FCSTD DOCUMENT  (FreeCAD 0.15R4671 (Git))
Label: Poliphemo
License: CreativeCommons Attribution-ShareAlike
LicenseURL: http://creativecommons.org/licenses/by-sa/4.0/
objects: Part::Cut×70, Part::Feature×40, Part::Cylinder×36, Part::FeaturePython×29, Part::Box×22, Part::MultiFuse×21, Sketcher::SketchObject×14, PartDesign::Pad×12, App::DocumentObjectGroup×12, Part::Fillet×6, Part::Prism×3, Part::Torus×2, Part::Extrusion×2, PartDesign::Revolution×2, Part::Offset×2, Part::Mirroring×1, Mesh::Feature×1
note: 276 computed .brp shape members not serialized (recipe doc carries the construction recipe); baked Part::Feature solids carry a one-line shape summary decoded from their .brp

FEATURE [Sketcher::SketchObject] Sketch
  Placement = pos=(0,0,0) rot=(1,0,0;1.5708rad)
  sketch-geometry (21):
    g0: LineSegment StartX=59.0543 StartY=-10.7909 StartZ=0 EndX=-13.0001 EndY=-10.7909 EndZ=0
    g1: LineSegment StartX=-15.0001 StartY=-12.7909 StartZ=0 EndX=-15.0001 EndY=-13.1898 EndZ=0
    g2: LineSegment StartX=-15 StartY=-20 StartZ=0 EndX=-18.8946 EndY=-20 EndZ=0
    g3: LineSegment StartX=-35 StartY=-13.1889 StartZ=0 EndX=-35 EndY=11.0101 EndZ=0
    g4: LineSegment StartX=-30 StartY=16.0101 StartZ=0 EndX=-9.59477 EndY=16.0101 EndZ=0
    g5: LineSegment StartX=39.6313 StartY=31.2232 StartZ=0 EndX=53.9362 EndY=56 EndZ=0
    g6: LineSegment StartX=74.9966 StartY=44.5054 StartZ=0 EndX=62.8248 EndY=20.8731 EndZ=0
    g7: LineSegment StartX=59.0543 StartY=5.31798 StartZ=0 EndX=59.0543 EndY=-10.7909 EndZ=0
    g8: Circle CenterX=-25 CenterY=-11.9899 CenterZ=0 NormalX=0 NormalY=0 NormalZ=1 Radius=2
    g9: Circle CenterX=64.3285 CenterY=50 CenterZ=0 NormalX=0 NormalY=0 NormalZ=1 Radius=2
    g10: Circle CenterX=35.461 CenterY=0 CenterZ=0 NormalX=0 NormalY=0 NormalZ=1 Radius=3.1
    g11: LineSegment [constr] StartX=35.461 StartY=0 StartZ=0 EndX=64.3285 EndY=50 EndZ=0
    g12: LineSegment [constr] StartX=51.5443 StartY=57.3809 StartZ=0 EndX=80.72 EndY=40.5364 EndZ=0
    g13: ArcOfCircle CenterX=64.3285 CenterY=50 CenterZ=0 NormalX=0 NormalY=0 NormalZ=1 Radius=12 StartAngle=5.80757 EndAngle=8.90118
    g14: ArcOfCircle CenterX=-30 CenterY=11.0101 CenterZ=0 NormalX=0 NormalY=0 NormalZ=1 Radius=5 StartAngle=1.5708 EndAngle=3.14159
    g15: ArcOfCircle CenterX=93.0258 CenterY=5.31798 CenterZ=0 NormalX=0 NormalY=0 NormalZ=1 Radius=33.9715 StartAngle=2.66598 EndAngle=3.14159
    g16: LineSegment StartX=1.09718 StartY=17.2548 StartZ=0 EndX=30.0327 EndY=24.0842 EndZ=0
    g17: ArcOfCircle CenterX=26.5676 CenterY=38.7656 CenterZ=0 NormalX=0 NormalY=0 NormalZ=1 Radius=15.0848 StartAngle=4.94417 EndAngle=5.75959
    g18: ArcOfCircle CenterX=-9.59477 CenterY=62.5551 CenterZ=0 NormalX=0 NormalY=0 NormalZ=1 Radius=46.545 StartAngle=4.71239 EndAngle=4.94417
    g19: ArcOfCircle CenterX=-25 CenterY=-11.9899 CenterZ=0 NormalX=0 NormalY=0 NormalZ=1 Radius=10.0716 StartAngle=3.26092 EndAngle=6.16376
    g20: ArcOfCircle CenterX=-13.0001 CenterY=-12.7909 CenterZ=0 NormalX=0 NormalY=0 NormalZ=1 Radius=2 StartAngle=1.5708 EndAngle=3.14159
  constraints (48):
    c: Horizontal(g0)
    c: Vertical(g1)
    c: Horizontal(g2)
    c: Vertical(g3)
    c: Horizontal(g4)
    c: Coincident(g7,g0)
    c: Radius(g8) = 2
    c: Radius(g9) = 2
    c: DistanceY(g-1,g9) = 50
    c: PointOnObject(g10,g-1)
    c: Radius(g10) = 3.1
    c: DistanceX(g-1,g8) = -25
    c: DistanceY(g-1,g8) = -11.9899
    c: DistanceX(g-1,g10) = 35.461
    c: DistanceY(g-1,g2) = -20
    c: Vertical(g7)
    c: DistanceX(g-1,g2) = -15
    c: Coincident(g11,g10)
    c: Coincident(g11,g9)
    c: DistanceY(g-1,g0) = -10.7909
    c: Angle(g11,g-1) = 2.0944
    c: Perpendicular(g11,g12)
    c: PointOnObject(g9,g12)
    c: Coincident(g13,g9)
    c: PointOnObject(g13,g5)
    c: PointOnObject(g5,g12)
    c: Tangent(g3,g14) = 1.5708
    c: Tangent(g4,g14) = 1.5708
    c: Tangent(g6,g15) = -1.5708
    c: Tangent(g7,g15) = -1.5708
    c: Tangent(g5,g13)
    c: Tangent(g6,g13)
    c: Coincident(g13,g6)
    c: Radius(g14) = 5
    c: Coincident(g5,g13)
    c: Radius(g13) = 12
    c: Tangent(g5,g17) = -1.5708
    c: Tangent(g16,g17) = -1.5708
    c: Tangent(g16,g18) = -1.5708
    c: Tangent(g4,g18) = -1.5708
    c: Coincident(g19,g8)
    c: PointOnObject(g2,g19)
    c: Coincident(g19,g1)
    c: Coincident(g3,g19)
    c: DistanceY(g4,g8) = -28
    c: Tangent(g1,g20) = -1.5708
    c: Tangent(g0,g20) = -1.5708
    c: Radius(g20) = 2
FEATURE [PartDesign::Pad] Pad
  Length = 4
  Length2 = 100
  Placement = pos=(0,0,0) rot=(1,0,0;1.5708rad)
  Sketch = -> Sketch
  Type = 0
FEATURE [Part::Box] Box  label="Cubo"
  Height = 30
  Length = 41.5
  Placement = pos=(4.2,-9,-19.6) rot=(0,0,1;0rad)
  Width = 20
FEATURE [Part::Cut] Cut
  Base = -> Pad
  Tool = -> Box
FEATURE [Sketcher::SketchObject] Sketch001
  Placement = pos=(0,0,0) rot=(0.57735,0.57735,0.57735;2.0944rad)
  sketch-geometry (5):
    g0: LineSegment StartX=-11.5774 StartY=37.7829 StartZ=0 EndX=-3.92366 EndY=37.7829 EndZ=0
    g1: LineSegment StartX=-3.92366 StartY=37.7829 StartZ=0 EndX=-3.92366 EndY=22.6692 EndZ=0
    g2: LineSegment StartX=-3.92366 StartY=22.6692 StartZ=0 EndX=-5.45233 EndY=33.3699 EndZ=0
    g3: LineSegment StartX=-7.03312 StartY=35.548 StartZ=0 EndX=-11.5774 EndY=37.7829 EndZ=0
    g4: ArcOfCircle CenterX=-8.30471 CenterY=32.9624 CenterZ=0 NormalX=0 NormalY=0 NormalZ=1 Radius=2.88134 StartAngle=0.141897 EndAngle=1.11373
  constraints (7):
    c: Horizontal(g0)
    c: Coincident(g0,g1)
    c: Vertical(g1)
    c: Coincident(g1,g2)
    c: Coincident(g3,g0)
    c: Tangent(g3,g4) = -1.5708
    c: Tangent(g2,g4) = -1.5708
FEATURE [PartDesign::Pad] Pad001
  Length = 3
  Length2 = 100
  Placement = pos=(0,0,0) rot=(0.57735,0.57735,0.57735;2.0944rad)
  Sketch = -> Sketch001
  Type = 0
FEATURE [Part::Fillet] Fillet
  Base = -> Pad001
  Edges = 6 edges r=1.1: [Edge9,Edge10,Edge12,Edge13,Edge14,Edge15]
  Placement = pos=(2,-33,4) rot=(0,0,1;0rad)
FEATURE [Part::FeaturePython] Clone  label="Clone of Fillet"  # Draft clone (typed FeaturePython)
  Objects = -> [Fillet]
  Placement = pos=(45.2816,0,3.93484) rot=(0,1,0;0.349066rad)
  Scale = (1,1,1)
FEATURE [Sketcher::SketchObject] Sketch002
  ExternalGeometry = -> [Cut]
  Placement = pos=(0,-4,0) rot=(1,0,0;1.5708rad)
  Support = -> Cut [Face5]
  sketch-geometry (2):
    g0: Circle CenterX=64.3285 CenterY=50 CenterZ=0 NormalX=0 NormalY=0 NormalZ=1 Radius=12
    g1: Circle CenterX=-25 CenterY=-11.9899 CenterZ=0 NormalX=0 NormalY=0 NormalZ=1 Radius=10.0716
  constraints (4):
    c: Coincident(g0,g-4)
    c: Coincident(g1,g-6)
    c: PointOnObject(g-6,g1)
    c: Radius(g0) = 12
FEATURE [PartDesign::Pad] Pad002
  Length = 13
  Length2 = 100
  Sketch = -> Sketch002
  Type = 0
FEATURE [Part::Cylinder] Cylinder  label="Cilindro"
  Angle = 360
  Height = 30
  Placement = pos=(-25,4,-12) rot=(1,0,0;1.5708rad)
  Radius = 2
FEATURE [Part::Cylinder] Cylinder001  label="Cilindro001"
  Angle = 360
  Height = 30
  Placement = pos=(64.33,4,50) rot=(1,0,0;1.5708rad)
  Radius = 2
FEATURE [Part::Cut] Cut001
  Base = -> Pad002
  Tool = -> Cylinder001
FEATURE [Part::Cut] Cut002
  Base = -> Cut001
  Tool = -> Cylinder
FEATURE [Part::MultiFuse] Fusion
  Shapes = -> [Cut002,Clone]
FEATURE [Part::Cylinder] Cylinder002  label="Cilindro002"
  Angle = 360
  Height = 30
  Placement = pos=(50.1,14,5.1) rot=(1,0,0;1.5708rad)
  Radius = 2
FEATURE [Part::Cylinder] Cylinder003  label="Cilindro003"
  Angle = 360
  Height = 30
  Placement = pos=(50.1,14,-5.1) rot=(1,0,0;1.5708rad)
  Radius = 2
FEATURE [Part::Cylinder] Cylinder004  label="Cilindro004"
  Angle = 360
  Height = 30
  Placement = pos=(-0.1,14,5.1) rot=(1,0,0;1.5708rad)
  Radius = 2
FEATURE [Part::Cylinder] Cylinder005  label="Cilindro005"
  Angle = 360
  Height = 30
  Placement = pos=(-0.1,14,-5.1) rot=(1,0,0;1.5708rad)
  Radius = 2
FEATURE [Part::Cut] Cut003
  Base = -> Fusion
  Tool = -> Cylinder002
FEATURE [Part::Cut] Cut004
  Base = -> Cut003
  Tool = -> Cylinder003
FEATURE [Part::Cut] Cut005
  Base = -> Cut004
  Tool = -> Cylinder004
FEATURE [Part::Cut] Cut006  label="preLatDer"
  Base = -> Cut005
  Tool = -> Cylinder005
FEATURE [Part::Prism] Prism  label="Prisma001"
  Circumradius = 3.35
  Height = 2.25
  Placement = pos=(0,-10,0) rot=(0,0,1;0rad)
  Polygon = 6
FEATURE [Part::Cylinder] Cylinder006  label="Cilindro023"
  Angle = 360
  Height = 30
  Placement = pos=(6e-12,-10,2.25) rot=(0,0,1;0rad)
  Radius = 2
FEATURE [Part::MultiFuse] Fusion001  label="taladroTuerca"
  Placement = pos=(-25,-17.1,-22) rot=(-1,0,0;1.5708rad)
  Shapes = -> [Prism,Cylinder006]
FEATURE [Part::FeaturePython] Clone001  label="Clone of taladroTuerca"  # Draft clone (typed FeaturePython)
  Objects = -> [Fusion001]
  Placement = pos=(64.33,-17.1,40) rot=(-1,0,0;1.5708rad)
  Scale = (1,1,1)
FEATURE [Part::FeaturePython] Clone002  label="Clone of taladroTuerca001"  # Draft clone (typed FeaturePython)
  Objects = -> [Fusion001]
  Placement = pos=(64.33,0.1,60) rot=(1,0,0;1.5708rad)
  Scale = (1,1,1)
FEATURE [Part::FeaturePython] Clone003  label="Clone of Clone of taladroTuerca001"  # Draft clone (typed FeaturePython)
  Objects = -> [Clone002]
  Placement = pos=(-25,0.1,-2) rot=(1,0,0;1.5708rad)
  Scale = (1,1,1)
FEATURE [Part::Cut] Cut007
  Base = -> Cut006
  Tool = -> Fusion001
FEATURE [Part::Cut] Cut008
  Base = -> Cut007
  Tool = -> Clone001
FEATURE [Part::Cut] Cut009
  Base = -> Cut008
  Tool = -> Clone002
FEATURE [Part::Cut] Cut010  label="preLateralDer"
  Base = -> Cut009
  Tool = -> Clone003
FEATURE [Part::Torus] Torus  label="Toro"
  Angle1 = -180
  Angle2 = 180
  Angle3 = 360
  Placement = pos=(64.3285,-16.5,50) rot=(1,0,0;1.5708rad)
  Radius1 = 7
  Radius2 = 1
FEATURE [Part::Torus] Torus001  label="Toro001"
  Angle1 = -180
  Angle2 = 180
  Angle3 = 360
  Placement = pos=(-25,-16.5,-11.9899) rot=(1,0,0;1.5708rad)
  Radius1 = 7
  Radius2 = 1
FEATURE [Part::MultiFuse] Fusion002
  Placement = pos=(-107.086,-40.5213,45) rot=(0,0,1;0rad)
  Shapes = -> [Cut010,Torus,Torus001]
FEATURE [Part::FeaturePython] Clone004  label="Clone of taladroTuerca004"  # WARN: FeaturePython — macro-defined, semantics opaque (R4)
  Placement = pos=(-24,12.1,16) rot=(1,0,0;1.5708rad)
  Scale = (1,1,1)
FEATURE [Part::FeaturePython] Clone005  label="Clone of Clone of taladroTuerca003"  # WARN: FeaturePython — macro-defined, semantics opaque (R4)
  Placement = pos=(49,3.1,41) rot=(1,0,0;1.5708rad)
  Scale = (1,1,1)
FEATURE [Part::Cut] Cut011
  Base = -> Fusion002
  Tool = -> Clone004
FEATURE [Part::Cut] Cut012  label="LateralDer"
  Base = -> Cut011
  Tool = -> Clone005
FEATURE [Part::FeaturePython] Clone006  label="Clone of preLatDerV5"  # Draft clone (typed FeaturePython)
  Objects = -> [Cut012]
  Scale = (1,1,1)
FEATURE [Part::Mirroring] Part__Mirroring  label="LateralIzq"
  Base = (20.7079,1.90735e-06,20.0487)
  Normal = (0,1,-1.19209e-07)
  Placement = pos=(0,64,0) rot=(0,0,1;0rad)
  Source = -> Clone006
FEATURE [App::DocumentObjectGroup] Grupo001  label="Gr_AuxLateral"
  Group = -> [Cut,Fillet]
FEATURE [App::DocumentObjectGroup] Grupo  label="GR_Laterales"
  Group = -> [Cut012,Part__Mirroring,Grupo001]
FEATURE [Part::Feature] Cut013  label="csLateralDer"
  shape: bbox 111.4 x 17.5 x 84.06 mm, 81 faces (baked)
FEATURE [Part::Feature] Part__Mirroring001  label="csLateralIzq"
  Placement = pos=(0,63,0) rot=(0,0,1;0rad)
  shape: bbox 111.4 x 17.5 x 84.06 mm, 81 faces (baked)
FEATURE [Part::Feature] Fusion003  label="csBaseV5"
  shape: bbox 114 x 63 x 24 mm, 132 faces (baked)
FEATURE [Part::Cylinder] Cylinder007  label="Cilindro024"
  Angle = 360
  Height = 19
  Placement = pos=(-46.35,14,0) rot=(0,0,1;0rad)
  Radius = 1
FEATURE [Part::Box] Box001  label="Cubo019"
  Height = 10
  Length = 9
  Placement = pos=(-31,0,-18) rot=(0,0,1;0rad)
  Width = 4
FEATURE [Part::Box] Box002  label="Cubo020"
  Height = 10
  Length = 9
  Placement = pos=(-31,59,-18) rot=(0,0,1;0rad)
  Width = 4
FEATURE [Part::Cut] Cut014
  Base = -> Fusion003
  Tool = -> Box001
FEATURE [Part::Cut] Cut015
  Base = -> Cut014
  Tool = -> Box002
FEATURE [Part::Box] Box003  label="Cubo021"
  Height = 20
  Length = 35
  Placement = pos=(6,14,0) rot=(0,0,1;0rad)
  Width = 35
FEATURE [Part::Fillet] Fillet001
  Base = -> Box003
  Edges = 4 edges r=10: [Edge1,Edge3,Edge5,Edge7]
FEATURE [Part::Cut] Cut016
  Base = -> Cut015
  Tool = -> Fillet001
FEATURE [Part::Cut] Cut017
  Base = -> Cut016
  Placement = pos=(2,-33,4) rot=(0,0,1;0rad)
  Tool = -> Cylinder007
FEATURE [Part::Box] Box004  label="Cubo022"
  Height = 5
  Length = 4
  Placement = pos=(-56.5,15.3,2) rot=(0,0,1;0rad)
  Width = 25
FEATURE [Part::Box] Box005  label="Cubo023"
  Height = 5
  Length = 4
  Placement = pos=(-40,15.3,2) rot=(0,0,1;0rad)
  Width = 25
FEATURE [Part::MultiFuse] Fusion004  label="Base"
  Placement = pos=(0,0,0) rot=(1,0,0;3.14159rad)
  Shapes = -> [Cut017,Box004,Box005]
FEATURE [Part::Box] Box006  label="Cubo001"
  Height = 4
  Length = 80
  Placement = pos=(-25.3,0,11) rot=(0,0,1;0rad)
  Width = 63
FEATURE [Part::Box] Box007  label="Cubo002"
  Height = 20
  Length = 9
  Placement = pos=(-5.3,0,-9) rot=(0,0,1;0rad)
  Width = 9
FEATURE [Part::FeaturePython] Clone007  label="Clone of Cubo002"  # Draft clone (typed FeaturePython)
  Objects = -> [Box007]
  Placement = pos=(-5.3,54,-9) rot=(0,0,1;0rad)
  Scale = (1,1,1)
FEATURE [Part::FeaturePython] Clone008  label="Clone of Cubo003"  # Draft clone (typed FeaturePython)
  Objects = -> [Box007]
  Placement = pos=(45.7,54,-9) rot=(0,0,1;0rad)
  Scale = (1,1,1)
FEATURE [Part::FeaturePython] Clone009  label="Clone of Cubo004"  # Draft clone (typed FeaturePython)
  Objects = -> [Box007]
  Placement = pos=(45.7,0,-9) rot=(0,0,1;0rad)
  Scale = (1,1,1)
FEATURE [Part::MultiFuse] Fusion005  label="preAlojaSer"
  Placement = pos=(0.25,0,0) rot=(0,0,1;0rad)
  Shapes = -> [Box006,Clone008,Clone007,Clone009,Box007]
FEATURE [Part::Cylinder] Cylinder008  label="Cilindro006"
  Angle = 360
  Height = 30
  Placement = pos=(50.1,14,5.1) rot=(1,0,0;1.5708rad)
  Radius = 2
FEATURE [Part::Cylinder] Cylinder009  label="Cilindro007"
  Angle = 360
  Height = 30
  Placement = pos=(50.1,14,-5.1) rot=(1,0,0;1.5708rad)
  Radius = 2
FEATURE [Part::Cylinder] Cylinder010  label="Cilindro008"
  Angle = 360
  Height = 30
  Placement = pos=(-0.1,14,5.1) rot=(1,0,0;1.5708rad)
  Radius = 2
FEATURE [Part::Cylinder] Cylinder011  label="Cilindro009"
  Angle = 360
  Height = 30
  Placement = pos=(-0.1,14,-5.1) rot=(1,0,0;1.5708rad)
  Radius = 2
FEATURE [Part::Cylinder] Cylinder012  label="Cilindro010"
  Angle = 360
  Height = 30
  Placement = pos=(50.1,76,5.1) rot=(1,0,0;1.5708rad)
  Radius = 2
FEATURE [Part::Cylinder] Cylinder013  label="Cilindro011"
  Angle = 360
  Height = 30
  Placement = pos=(50.1,76,-5.1) rot=(1,0,0;1.5708rad)
  Radius = 2
FEATURE [Part::Cylinder] Cylinder014  label="Cilindro012"
  Angle = 360
  Height = 30
  Placement = pos=(-0.1,76,5.1) rot=(1,0,0;1.5708rad)
  Radius = 2
FEATURE [Part::Cylinder] Cylinder015  label="Cilindro013"
  Angle = 360
  Height = 30
  Placement = pos=(-0.1,76,-5.1) rot=(1,0,0;1.5708rad)
  Radius = 2
FEATURE [Part::Cut] Cut018
  Base = -> Fusion005
  Tool = -> Cylinder008
FEATURE [Part::Cut] Cut019
  Base = -> Cut018
  Tool = -> Cylinder009
FEATURE [Part::Cut] Cut020
  Base = -> Cut019
  Placement = pos=(2,-33,4) rot=(0,0,1;0rad)
  Tool = -> Cylinder010
FEATURE [Part::Cut] Cut021
  Base = -> Cut020
  Placement = pos=(2,-33,4) rot=(0,0,1;0rad)
  Tool = -> Cylinder011
FEATURE [Part::Cut] Cut022
  Base = -> Cut021
  Tool = -> Cylinder012
FEATURE [Part::Cut] Cut023
  Base = -> Cut022
  Tool = -> Cylinder013
FEATURE [Part::Cut] Cut024
  Base = -> Cut023
  Tool = -> Cylinder014
FEATURE [Part::Cut] Cut025  label="preAlojaSer2"
  Base = -> Cut024
  Tool = -> Cylinder015
FEATURE [Part::Box] Box008  label="Hueco_Cuerpo_Tuerca_4"
  Height = 6
  Length = 62
  Placement = pos=(-6,3,2.1) rot=(0,0,1;0rad)
  Width = 3
FEATURE [Part::Box] Box009  label="Hueco_Cuerpo_Tuerca_005"
  Height = 6
  Length = 62
  Placement = pos=(-6,3,-8.1) rot=(0,0,1;0rad)
  Width = 3
FEATURE [Part::Box] Box010  label="Hueco_Cuerpo_Tuerca_006"
  Height = 6
  Length = 62
  Placement = pos=(-6,57,2.1) rot=(0,0,1;0rad)
  Width = 3
FEATURE [Part::Box] Box011  label="Hueco_Cuerpo_Tuerca_007"
  Height = 6
  Length = 62
  Placement = pos=(-6,57,-8.1) rot=(0,0,1;0rad)
  Width = 3
FEATURE [Part::Cut] Cut026
  Base = -> Cut025
  Tool = -> Box008
FEATURE [Part::Cut] Cut027
  Base = -> Cut026
  Tool = -> Box009
FEATURE [Part::Cut] Cut028
  Base = -> Cut027
  Tool = -> Box010
FEATURE [Part::Cut] Cut029  label="preAlojaSer3"
  Base = -> Cut028
  Tool = -> Box011
FEATURE [Part::Box] Box012  label="Cubo024"
  Height = 4
  Length = 35
  Placement = pos=(-59,0,11) rot=(0,0,1;0rad)
  Width = 63
FEATURE [Part::Cylinder] Cylinder016  label="Cilindro019"
  Angle = 360
  Height = 40
  Placement = pos=(-11.05,6,1) rot=(0,0,1;0rad)
  Radius = 2
FEATURE [Part::Cylinder] Cylinder017  label="Cilindro020"
  Angle = 360
  Height = 40
  Placement = pos=(-11.05,57,1) rot=(0,0,1;0rad)
  Radius = 2
FEATURE [Part::Cut] Cut030
  Base = -> Cut029
  Tool = -> Cylinder017
FEATURE [Part::Cut] Cut031
  Base = -> Cut030
  Tool = -> Cylinder016
FEATURE [Part::Box] Box013  label="Cubo011"
  Height = 12.5
  Length = 23.3
  Placement = pos=(-52.5,15.8,20.4) rot=(0,1,0;1.5708rad)
  Width = 24
FEATURE [Part::Feature] Pad003
  Placement = pos=(-12,31.5,7) rot=(0,0,1;0rad)
  shape: bbox 10 x 25 x 20 mm, 6 faces (baked)
FEATURE [Part::Cylinder] Cylinder018  label="Cilindro025"
  Angle = 360
  Height = 10
  Placement = pos=(-46,39.8,5) rot=(0,0,1;0rad)
  Radius = 2
FEATURE [Part::Fillet] Fillet002
  Base = -> Box012
  Edges = 2 edges r=20: [Edge1,Edge3]
FEATURE [Part::MultiFuse] Fusion006
  Shapes = -> [Cut031,Fillet002]
FEATURE [Part::Cut] Cut032
  Base = -> Fusion006
  Tool = -> Box013
FEATURE [Part::Cut] Cut033
  Base = -> Cut032
  Placement = pos=(0,0,-4) rot=(0,0,1;0rad)
  Tool = -> Pad003
FEATURE [Part::Cut] Cut034
  Base = -> Cut033
  Tool = -> Cylinder018
FEATURE [Part::Prism] Prism001  label="Prisma002"
  Circumradius = 3.35
  Height = 2.25
  Placement = pos=(0,-10,0) rot=(0,0,1;0rad)
  Polygon = 6
FEATURE [Part::Cylinder] Cylinder019  label="Cilindro026"
  Angle = 360
  Height = 30
  Placement = pos=(6e-12,-10,2.25) rot=(0,0,1;0rad)
  Radius = 2
FEATURE [Part::MultiFuse] Fusion007  label="taladroTuerca001"
  Placement = pos=(-24,12.1,12) rot=(1,0,0;1.5708rad)
  Shapes = -> [Prism001,Cylinder019]
FEATURE [Part::FeaturePython] Clone010  label="Clone of taladroTuerca005"  # Draft clone (typed FeaturePython)
  Objects = -> [Fusion007]
  Placement = pos=(-24,50.9,-8) rot=(-1,0,0;1.5708rad)
  Scale = (1,1,1)
FEATURE [Part::Box] Box014  label="Cubo012"
  Height = 13
  Length = 25
  Placement = pos=(-30,0,-6) rot=(0,0,1;0rad)
  Width = 12
FEATURE [Part::Box] Box015  label="Cubo013"
  Height = 3
  Length = 6
  Placement = pos=(-14.05,43.0988,1) rot=(0,0,1;0rad)
  Width = 22
FEATURE [Part::Box] Box016  label="Cubo014"
  Height = 13
  Length = 25
  Placement = pos=(-30.05,51,-6) rot=(0,0,1;0rad)
  Width = 12
FEATURE [Part::Box] Box017  label="Cubo015"
  Height = 3
  Length = 6
  Placement = pos=(-14.05,-6,1) rot=(0,0,1;0rad)
  Width = 22
FEATURE [Part::Cut] Cut035
  Base = -> Box016
  Tool = -> Box015
FEATURE [Part::Cut] Cut036
  Base = -> Box014
  Tool = -> Box017
FEATURE [Part::MultiFuse] Fusion008  label="taladroTuerca002"
  Placement = pos=(-11.05,-4,21.25) rot=(1,0,0;3.14159rad)
  Shapes = -> [Prism001,Cylinder019]
FEATURE [Part::FeaturePython] Clone011  label="Clone of taladroTuerca006"  # Draft clone (typed FeaturePython)
  Objects = -> [Fusion008]
  Placement = pos=(-11.05,47,21.25) rot=(1,0,0;3.14159rad)
  Scale = (1,1,1)
FEATURE [Part::Cut] Cut037
  Base = -> Cut036
  Tool = -> Fusion008
FEATURE [Part::Cut] Cut038
  Base = -> Cut035
  Tool = -> Clone011
FEATURE [Part::Cut] Cut039
  Base = -> Cut037
  Tool = -> Fusion007
FEATURE [Part::Cut] Cut040
  Base = -> Cut038
  Tool = -> Clone010
FEATURE [Part::MultiFuse] Fusion009  label="BaseV4"
  Shapes = -> [Cut034,Cut039,Cut040]
FEATURE [Part::Feature] Pad004
  Placement = pos=(-30.05,-0.115984,0.0102208) rot=(0.57735,0.57735,0.57735;2.0944rad)
  shape: bbox 25 x 12 x 7 mm, 8 faces (baked)
FEATURE [Part::Feature] Pad005
  Placement = pos=(-30.05,63.116,-19.0102) rot=(0.57735,-0.57735,0.57735;4.18879rad)
  shape: bbox 25 x 12 x 7 mm, 8 faces (baked)
FEATURE [Part::MultiFuse] Fusion010  label="BaseV5"
  Shapes = -> [Fusion009,Pad004,Pad005]
FEATURE [Sketcher::SketchObject] Sketch003
  Placement = pos=(-30,0,0) rot=(0.57735,0.57735,0.57735;2.0944rad)
  sketch-geometry (6):
    g0: LineSegment StartX=0.115984 StartY=-13.0102 StartZ=0 EndX=12.116 EndY=-13.0102 EndZ=0
    g1: LineSegment StartX=12.116 StartY=-13.0102 StartZ=0 EndX=8.96276 EndY=-9.857 EndZ=0
    g2: LineSegment StartX=8.96276 StartY=-9.857 StartZ=0 EndX=8.96276 EndY=-9.16345 EndZ=0
    g3: LineSegment StartX=8.96276 StartY=-9.16345 StartZ=0 EndX=12.116 EndY=-6.01022 EndZ=0
    g4: LineSegment StartX=12.116 StartY=-6.01022 StartZ=0 EndX=0.115984 EndY=-6.01022 EndZ=0
    g5: LineSegment StartX=0.115984 StartY=-6.01022 StartZ=0 EndX=0.115984 EndY=-13.0102 EndZ=0
  constraints (15):
    c: Coincident(g1,g2)
    c: Coincident(g2,g3)
    c: Coincident(g3,g4)
    c: Coincident(g4,g5)
    c: Coincident(g5,g0)
    c: Horizontal(g0)
    c: Coincident(g1,g0)
    c: Vertical(g5)
    c: DistanceY(g5) = -7
    c: Horizontal(g4)
    c: DistanceX(g0) = 12
    c: Equal(g0,g4)
    c: Angle(g4,g3) = 0.785398
    c: Angle(g1,g0) = 0.785398
    c: Vertical(g2)
FEATURE [PartDesign::Pad] Pad006  label="muesca"
  Length = 25
  Length2 = 100
  Placement = pos=(-30,0,0) rot=(0.57735,0.57735,0.57735;2.0944rad)
  Sketch = -> Sketch003
  Type = 0
FEATURE [App::DocumentObjectGroup] Grupo003  label="GR_AuxBase"
  Group = -> [Fusion010,Pad006]
FEATURE [App::DocumentObjectGroup] Grupo002  label="GR_Base"
  Group = -> [Grupo003,Fusion004]
FEATURE [Part::Feature] Fusion011  label="csBase"
  Placement = pos=(0,0,4) rot=(0,0,1;0rad)
  shape: bbox 114 x 63 x 24 mm, 155 faces (baked)
FEATURE [Part::Box] Box018  label="Cubo005"
  Height = 30
  Length = 60
  Placement = pos=(-5,0,14) rot=(0,0,1;0rad)
  Width = 63
FEATURE [Part::Box] Box019  label="Cubo006"
  Height = 39
  Length = 63
  Placement = pos=(-11,3,11) rot=(0,0,1;0rad)
  Width = 57
FEATURE [Part::Cut] Cut041  label="preAlojaPilas1"
  Base = -> Box018
  Placement = pos=(50,63,0) rot=(0,0,1;3.14159rad)
  Tool = -> Box019
FEATURE [Part::Box] Box020  label="Cubo018"
  Height = 5
  Length = 60
  Width = 63
FEATURE [Part::Feature] Face
  shape: bbox 41.8 x 19.8 x 2e-07 mm, 1 faces, 0 solids (baked)
FEATURE [Part::Extrusion] Extrude
  Base = -> Face
  Dir = (0,0,8)
  Placement = pos=(-6,92,-43) rot=(0,0,1;0rad)
  Solid = true
FEATURE [Part::Extrusion] Extrude001
  Base = -> Face
  Dir = (0,0,8)
  Placement = pos=(66,-29,-43) rot=(0,0,1;3.14159rad)
  Solid = true
FEATURE [Part::FeaturePython] Clone012  label="Clone of Extrude003"  # Draft clone (typed FeaturePython)
  Objects = -> [Extrude001]
  Placement = pos=(89,67.5,-43) rot=(0,0,-1;1.5708rad)
  Scale = (1,1,1)
FEATURE [Part::FeaturePython] Clone013  label="Clone of Extrude004"  # Draft clone (typed FeaturePython)
  Objects = -> [Extrude001]
  Placement = pos=(-29,-4.5,-43) rot=(0,0,1;1.5708rad)
  Scale = (1,1,1)
FEATURE [Part::Cut] Cut042
  Base = -> Box020
  Tool = -> Extrude
FEATURE [Part::Cut] Cut043
  Base = -> Cut042
  Tool = -> Extrude001
FEATURE [Part::Cut] Cut044
  Base = -> Cut043
  Tool = -> Clone012
FEATURE [Part::Cut] Cut045
  Base = -> Cut044
  Tool = -> Clone013
FEATURE [Part::Cylinder] Cylinder020  label="Cilindro027"
  Angle = 360
  Height = 10
  Placement = pos=(20.0282,41.5321,-3) rot=(0,0,1;0rad)
  Radius = 2
FEATURE [Part::Cylinder] Cylinder021  label="Cilindro028"
  Angle = 360
  Height = 10
  Placement = pos=(40.0282,41.5321,-3) rot=(0,0,1;0rad)
  Radius = 2
FEATURE [Part::Cylinder] Cylinder022  label="Cilindro021"
  Angle = 360
  Height = 10
  Placement = pos=(20.0282,21.5321,-3) rot=(0,0,1;0rad)
  Radius = 2
FEATURE [Part::Cylinder] Cylinder023  label="Cilindro022"
  Angle = 360
  Height = 10
  Placement = pos=(40.0282,21.5321,-3) rot=(0,0,1;0rad)
  Radius = 2
FEATURE [Part::Cut] Cut046
  Base = -> Cut045
  Tool = -> Cylinder020
FEATURE [Part::Cut] Cut047
  Base = -> Cut046
  Tool = -> Cylinder021
FEATURE [Part::Cut] Cut048
  Base = -> Cut047
  Tool = -> Cylinder022
FEATURE [Part::Cut] Cut049
  Base = -> Cut048
  Tool = -> Cylinder023
FEATURE [Part::Prism] Prism002  label="Prisma003"
  Circumradius = 3.35
  Height = 2.25
  Placement = pos=(0,-10,0) rot=(0,0,1;0rad)
  Polygon = 6
FEATURE [Part::Cylinder] Cylinder024  label="Cilindro029"
  Angle = 360
  Height = 10
  Placement = pos=(6e-12,-10,2.25) rot=(0,0,1;0rad)
  Radius = 2
FEATURE [Part::MultiFuse] Fusion012
  Placement = pos=(20.0282,31.5321,-0.05) rot=(0,0,1;0rad)
  Shapes = -> [Prism002,Cylinder024]
FEATURE [Part::FeaturePython] Clone014  label="Clone of Fusion003"  # Draft clone (typed FeaturePython)
  Objects = -> [Fusion012]
  Placement = pos=(40.0282,31.5321,-0.05) rot=(0,0,1;0rad)
  Scale = (1,1,1)
FEATURE [Part::FeaturePython] Clone015  label="Clone of Fusion004"  # Draft clone (typed FeaturePython)
  Objects = -> [Fusion012]
  Placement = pos=(40.0282,51.5321,-0.05) rot=(0,0,1;0rad)
  Scale = (1,1,1)
FEATURE [Part::FeaturePython] Clone016  label="Clone of Fusion005"  # Draft clone (typed FeaturePython)
  Objects = -> [Fusion012]
  Placement = pos=(20.0282,51.5321,-0.05) rot=(0,0,1;0rad)
  Scale = (1,1,1)
FEATURE [Part::Cut] Cut050
  Base = -> Cut049
  Tool = -> Fusion012
FEATURE [Part::Cut] Cut051
  Base = -> Cut050
  Tool = -> Clone014
FEATURE [Part::Cut] Cut052
  Base = -> Cut051
  Tool = -> Clone015
FEATURE [Part::Cut] Cut053  label="preXtap001"
  Base = -> Cut052
  Placement = pos=(-5,0,39) rot=(0,0,1;0rad)
  Tool = -> Clone016
FEATURE [Part::Cylinder] Cylinder025  label="Cilindro030"
  Angle = 180
  Height = 30
  Placement = pos=(-11,6,14) rot=(0,0,1;1.5708rad)
  Radius = 6
FEATURE [Part::Box] Box021  label="Cubo025"
  Height = 30
  Length = 12
  Placement = pos=(-5,0,14) rot=(0,0,1;1.5708rad)
  Width = 6
FEATURE [Part::Feature] Fusion013  label="csTaladro35x3"
  Placement = pos=(-11,6,47.5) rot=(1,0,0;3.14159rad)
  shape: bbox 5.8 x 5.8 x 38.5 mm, 5 faces (baked)
FEATURE [Part::MultiFuse] Fusion014
  Shapes = -> [Cylinder025,Box021]
FEATURE [Part::Cut] Cut054  label="FijaPieza2"
  Base = -> Fusion014
  Tool = -> Fusion013
FEATURE [Part::Feature] Cut055  label="FijaPieza1"
  Placement = pos=(0,51,0) rot=(0,0,1;0rad)
  shape: bbox 12 x 12 x 30 mm, 7 faces (baked)
FEATURE [Part::MultiFuse] Fusion015
  Shapes = -> [Cut041,Cut055,Cut054]
FEATURE [Part::MultiFuse] Fusion016
  Shapes = -> [Fusion015,Cut053]
FEATURE [Part::Fillet] Fillet003  label="TapaPilasV2"
  Base = -> Fusion016
  Edges = 2 edges r=5: [Edge39,Edge42]
FEATURE [Part::Feature] Fillet004  label="TapaPilasV003"
  shape: bbox 72 x 63 x 30 mm, 61 faces (baked)
FEATURE [Part::Feature] Clone017  label="ClonPoliphemoNom001"
  Placement = pos=(21,1,40) rot=(1,0,0;1.5708rad)
  shape: bbox 53.2 x 3 x 8.442 mm, 569 faces, 9 solids (baked)
FEATURE [Part::Cut] Cut056
  Base = -> Fillet004
  Placement = pos=(-0.05,0,-3) rot=(0,0,1;0rad)
  Tool = -> Clone017
FEATURE [Part::FeaturePython] Clone019  label="Clone of Clone of Clone of Clone of taladroTuerca"  # WARN: FeaturePython — macro-defined, semantics opaque (R4)
  Placement = pos=(49,59.9,21) rot=(-1,0,0;1.5708rad)
  Scale = (1,1,1)
FEATURE [Part::FeaturePython] Clone018  label="Clone of Clone of Clone of taladroTuerca002"  # Draft clone (typed FeaturePython)
  Objects = -> [Clone019]
  Placement = pos=(49,3.1,41) rot=(1,0,0;1.5708rad)
  Scale = (1,1,1)
FEATURE [Part::Cut] Cut057
  Base = -> Cut056
  Tool = -> Clone018
FEATURE [Part::Cut] Cut058  label="TapaAlojapilasV3"
  Base = -> Cut057
  Tool = -> Clone019
FEATURE [App::DocumentObjectGroup] Grupo004  label="GR_AlojapilasOld"
  Group = -> [Fillet003,Cut058]
FEATURE [Part::Feature] Fillet005  label="TapaPilasV004"
  shape: bbox 72 x 63 x 30 mm, 61 faces (baked)
FEATURE [Part::Feature] Clone020  label="ClonPoliphemoNom002"
  Placement = pos=(21,1,40) rot=(1,0,0;1.5708rad)
  shape: bbox 53.2 x 3 x 8.442 mm, 569 faces, 9 solids (baked)
FEATURE [Part::Cut] Cut059
  Base = -> Fillet005
  Placement = pos=(-2.05,33,-3) rot=(0,0,1;0rad)
  Tool = -> Clone020
FEATURE [Part::FeaturePython] Clone022  label="Clone of Clone of Clone of Clone of taladroTuerca001"  # WARN: FeaturePython — macro-defined, semantics opaque (R4)
  Placement = pos=(47,92.75,17) rot=(-1,0,0;1.5708rad)
  Scale = (1,1,1)
FEATURE [Part::FeaturePython] Clone021  label="Clone of Clone of Clone of taladroTuerca003"  # Draft clone (typed FeaturePython)
  Objects = -> [Clone022]
  Placement = pos=(47,36.25,37) rot=(1,0,0;1.5708rad)
  Scale = (1,1,1)
FEATURE [Part::Cut] Cut060
  Base = -> Cut059
  Tool = -> Clone021
FEATURE [Part::Cut] Cut061  label="TapaAlojapilasV4"
  Base = -> Cut060
  Placement = pos=(2,-33,4) rot=(0,0,1;0rad)
  Tool = -> Clone022
FEATURE [Part::Feature] Cut062  label="csAlojapilas"
  Placement = pos=(2,-33,4) rot=(0,0,1;0rad)
  shape: bbox 72 x 65 x 30 mm, 639 faces (baked)
FEATURE [App::DocumentObjectGroup] Grupo005  label="GR_AlojaPilas"
  Group = -> [Grupo004,Cut061]
FEATURE [Sketcher::SketchObject] Sketch004
  Placement = pos=(0,0,0) rot=(0.57735,0.57735,0.57735;2.0944rad)
  sketch-geometry (6):
    g0: LineSegment StartX=2.1 StartY=-10 StartZ=0 EndX=2.1 EndY=4 EndZ=0
    g1: LineSegment StartX=2.1 StartY=4 StartZ=0 EndX=3.5 EndY=4 EndZ=0
    g2: LineSegment StartX=3.5 StartY=4 StartZ=0 EndX=3.5 EndY=10 EndZ=0
    g3: LineSegment StartX=3.5 StartY=10 StartZ=0 EndX=13.8 EndY=10 EndZ=0
    g4: LineSegment StartX=13.8 StartY=10 StartZ=0 EndX=13.8 EndY=-10 EndZ=0
    g5: LineSegment StartX=13.8 StartY=-10 StartZ=0 EndX=2.1 EndY=-10 EndZ=0
  constraints (18):
    c: Coincident(g0,g1)
    c: Coincident(g1,g2)
    c: Coincident(g2,g3)
    c: Coincident(g3,g4)
    c: Coincident(g4,g5)
    c: Coincident(g5,g0)
    c: Horizontal(g5)
    c: Horizontal(g3)
    c: Vertical(g4)
    c: Vertical(g2)
    c: Vertical(g0)
    c: Horizontal(g1)
    c: DistanceY(g3,g4) = -20
    c: DistanceX(g-1,g4) = 13.8
    c: DistanceX(g-1,g0) = 2.1
    c: DistanceX(g-1,g2) = 3.5
    c: DistanceY(g2) = 6
    c: Symmetric(g3,g4,g-1)
FEATURE [PartDesign::Revolution] Revolution
  Angle = 360
  Axis = (0,0,1)
  Base = (0,0,0)
  Placement = pos=(0,0,0) rot=(0.57735,0.57735,0.57735;2.0944rad)
  ReferenceAxis = -> Sketch004 [V_Axis]
  Reversed = true
  Sketch = -> Sketch004
FEATURE [Sketcher::SketchObject] Sketch005
  Placement = pos=(0,0,-15) rot=(0,0,1;0rad)
  sketch-geometry (2):
    g0: Circle CenterX=0 CenterY=0 CenterZ=0 NormalX=0 NormalY=0 NormalZ=1 Radius=13.8
    g1: Circle CenterX=0 CenterY=0 CenterZ=0 NormalX=0 NormalY=0 NormalZ=1 Radius=17
  constraints (3):
    c: Coincident(g0,g-1)
    c: Radius(g0) = 13.8
    c: Radius(g1) = 17
FEATURE [PartDesign::Pad] Pad007
  Length = 30
  Length2 = 100
  Placement = pos=(0,0,-15) rot=(0,0,1;0rad)
  Sketch = -> Sketch005
  Type = 0
FEATURE [Part::FeaturePython] Clone023  label="Clone of Pad001"  # WARN: FeaturePython — macro-defined, semantics opaque (R4)
  Placement = pos=(0,0,-15) rot=(0,0,1;0rad)
  Scale = (1,1,1)
FEATURE [Part::FeaturePython] Array  # Draft array (typed FeaturePython)
  Angle = 360
  ArrayType = 1
  Axis = (0,0,1)
  Base = -> Clone023
  Center = (0,0,0)
  Fuse = false
  IntervalAxis = (0,0,0)
  IntervalX = (1,0,0)
  IntervalY = (0,1,0)
  IntervalZ = (0,0,0)
  NumberPolar = 8
  NumberX = 2
  NumberY = 2
  NumberZ = 1
FEATURE [Part::MultiFuse] Fusion017
  Shapes = -> [Pad007,Array]
FEATURE [Part::Cut] Cut063
  Base = -> Revolution
  Tool = -> Fusion017
FEATURE [Part::Fillet] Fillet006  label="ruedaPeq26"
  Base = -> Cut063
  Edges = 16 edges r=2.6: [Edge37,Edge43,Edge45,Edge51,Edge53,Edge59,Edge61,Edge67,Edge69,Edge75,Edge76,Edge83,Edge84,Edge91,Edge92,Edge99]
FEATURE [Part::Cylinder] Cylinder026  label="Cilindro031"
  Angle = 360
  Height = 1
  Placement = pos=(0,0,-11) rot=(0,0,1;0rad)
  Radius = 14.5
FEATURE [Part::Cylinder] Cylinder027  label="Cilindro032"
  Angle = 360
  Height = 10
  Placement = pos=(0,0,-16) rot=(0,0,1;0rad)
  Radius = 2.1
FEATURE [Part::Cut] Cut064
  Base = -> Cylinder026
  Tool = -> Cylinder027
FEATURE [Part::Cylinder] Cylinder028  label="Cilindro033"
  Angle = 360
  Height = 1
  Placement = pos=(0,0,-11) rot=(0,0,1;0rad)
  Radius = 14.5
FEATURE [Part::Cylinder] Cylinder029  label="Cilindro034"
  Angle = 360
  Height = 10
  Placement = pos=(0,0,-16) rot=(0,0,1;0rad)
  Radius = 3.5
FEATURE [Part::Cut] Cut065
  Base = -> Cylinder028
  Placement = pos=(0,0,21) rot=(0,0,1;0rad)
  Tool = -> Cylinder029
FEATURE [Part::FeaturePython] Clone024  label="Clone of ruedaPeq26"  # Draft clone (typed FeaturePython)
  Objects = -> [Fillet006]
  Scale = (1,1,1)
FEATURE [Part::MultiFuse] Fusion018  label="ruedaDentPeqTopes"
  Shapes = -> [Cut064,Cut065,Clone024]
FEATURE [App::DocumentObjectGroup] Grupo006  label="GR_RuedaPeq"
  Group = -> [Fillet006,Fusion018]
FEATURE [Part::Feature] Fusion019  label="csruedaDentPeq1"
  Placement = pos=(-25,-28.7,-11.9899) rot=(1,0,0;1.5708rad)
  shape: bbox 29 x 22 x 29 mm, 57 faces (baked)
FEATURE [Part::Feature] Fusion020  label="csruedaDentPeq2"
  Placement = pos=(64.3285,-28.7,50) rot=(1,0,0;1.5708rad)
  shape: bbox 29 x 22 x 29 mm, 57 faces (baked)
FEATURE [Part::Feature] Fusion021  label="csruedaDentPeq3"
  Placement = pos=(64.3285,91.7,50) rot=(0,0.707107,0.707107;3.14159rad)
  shape: bbox 29 x 22 x 29 mm, 57 faces (baked)
FEATURE [Part::Feature] Fusion022  label="csruedaDentPeq4"
  Placement = pos=(-25,91.7,-11.9899) rot=(0,0.707107,0.707107;3.14159rad)
  shape: bbox 29 x 22 x 29 mm, 57 faces (baked)
FEATURE [Part::Feature] Compound  label="ServoMG90S001"
  Placement = pos=(-32.1,25.8,42.7) rot=(0.57735,-0.57735,-0.57735;4.18879rad)
  shape: bbox 12.4 x 30.2 x 32.5 mm, 32 faces, 2 solids (baked)
FEATURE [Part::Feature] Compound001  label="ServoMG90S"
  Placement = pos=(-46.3,27.2,-0.9) rot=(0,0,-1;1.5708rad)
  shape: bbox 12.4 x 32.5 x 30.2 mm, 32 faces, 2 solids (baked)
FEATURE [Part::Feature] Cut066  label="forTilt002"
  Placement = pos=(-46.3,32.4,26.3) rot=(0.57735,-0.57735,-0.57735;2.0944rad)
  shape: bbox 50.58 x 52.96 x 11 mm, 101 faces (baked)
FEATURE [Part::Feature] Fusion023  label="prePortaCam003"
  Placement = pos=(-48.3,31.9,26.25) rot=(0,0,-1;1.5708rad)
  shape: bbox 13.33 x 53.91 x 19.33 mm, 65 faces (baked)
FEATURE [Part::Feature] Pad008  label="csSeparaPlaca"
  Placement = pos=(24.9782,31.5321,45) rot=(0,0,1;0rad)
  shape: bbox 28.03 x 28 x 3 mm, 18 faces (baked)
FEATURE [Part::Feature] Fusion024  label="csPixy"
  Placement = pos=(-72.3,31.901,42.2219) rot=(0.57735,-0.57735,-0.57735;2.0944rad)
  shape: bbox 22.9 x 53.85 x 50.8 mm, 52 faces (baked)
FEATURE [Part::Feature] Compound002  label="csServo-SM-S4303R_I"
  Placement = pos=(24.95,24.9,0) rot=(1,0,0;1.5708rad)
  shape: bbox 60.12 x 46.3 x 21.13 mm, 542 faces, 7 solids (baked)
FEATURE [Part::Feature] Compound003  label="Servo-SM-S4303R002"
  Placement = pos=(25.05,38.1,0) rot=(-1,0,0;1.5708rad)
  shape: bbox 60.12 x 46.3 x 21.13 mm, 542 faces, 7 solids (baked)
FEATURE [Sketcher::SketchObject] Sketch006
  Placement = pos=(0,0,0) rot=(-1,0,0;1.5708rad)
  sketch-geometry (7):
    g0: LineSegment StartX=4.5 StartY=12 StartZ=0 EndX=4.5 EndY=6 EndZ=0
    g1: LineSegment StartX=4.5 StartY=6 StartZ=0 EndX=17 EndY=6 EndZ=0
    g2: LineSegment StartX=20 StartY=3 StartZ=0 EndX=20 EndY=-12 EndZ=0
    g3: LineSegment StartX=20 StartY=-12 StartZ=0 EndX=26.5 EndY=-12 EndZ=0
    g4: LineSegment StartX=26.5 StartY=12 StartZ=0 EndX=4.5 EndY=12 EndZ=0
    g5: ArcOfCircle CenterX=17 CenterY=3 CenterZ=0 NormalX=0 NormalY=0 NormalZ=1 Radius=3 StartAngle=0 EndAngle=1.5708
    g6: LineSegment StartX=26.5 StartY=12 StartZ=0 EndX=26.5 EndY=-12 EndZ=0
  constraints (19):
    c: Vertical(g0)
    c: Coincident(g0,g1)
    c: Horizontal(g1)
    c: Vertical(g2)
    c: Coincident(g2,g3)
    c: Horizontal(g3)
    c: Coincident(g4,g0)
    c: Horizontal(g4)
    c: Symmetric(g4,g3,g-1)
    c: DistanceY(g0) = -6
    c: DistanceY(g4,g3) = -24
    c: DistanceX(g-1,g0) = 4.5
    c: DistanceX(g-1,g2) = 20
    c: DistanceX(g-1,g4) = 26.5
    c: Tangent(g1,g5) = 1.5708
    c: Tangent(g2,g5) = 1.5708
    c: Radius(g5) = 3
    c: Coincident(g6,g4)
    c: Coincident(g6,g3)
FEATURE [PartDesign::Revolution] Revolution001
  Angle = 360
  Axis = (0,0,-1)
  Base = (0,0,0)
  Placement = pos=(0,0,0) rot=(-1,0,0;1.5708rad)
  ReferenceAxis = -> Sketch006 [V_Axis]
  Reversed = true
  Sketch = -> Sketch006
FEATURE [Part::Feature] Fusion025  label="horn-body-003"
  Placement = pos=(0,0,-9.8) rot=(0,0,1;0rad)
  shape: bbox 38.8 x 38.8 x 32 mm, 26 faces (baked)
FEATURE [Sketcher::SketchObject] Sketch007
  Placement = pos=(0,0,-15) rot=(0,0,1;0rad)
  sketch-geometry (2):
    g0: Circle CenterX=0 CenterY=0 CenterZ=0 NormalX=0 NormalY=0 NormalZ=1 Radius=26.5
    g1: Circle CenterX=0 CenterY=0 CenterZ=0 NormalX=0 NormalY=0 NormalZ=1 Radius=35
  constraints (3):
    c: Coincident(g0,g-1)
    c: Radius(g0) = 26.5
    c: Radius(g1) = 35
FEATURE [PartDesign::Pad] Pad009
  Length = 30
  Length2 = 100
  Placement = pos=(0,0,-15) rot=(0,0,1;0rad)
  Sketch = -> Sketch007
  Type = 0
FEATURE [Sketcher::SketchObject] Sketch008
  sketch-geometry (8):
    g0: LineSegment StartX=28.5 StartY=2 StartZ=0 EndX=31.5 EndY=1.5 EndZ=0
    g1: LineSegment StartX=31.5 StartY=1.5 StartZ=0 EndX=31.5 EndY=-1.5 EndZ=0
    g2: LineSegment StartX=31.5 StartY=-1.5 StartZ=0 EndX=28.5 EndY=-2 EndZ=0
    g3: LineSegment StartX=28.5 StartY=2 StartZ=0 EndX=26.5 EndY=2 EndZ=0
    g4: LineSegment StartX=26.5 StartY=2 StartZ=0 EndX=23.5 EndY=1.5 EndZ=0
    g5: LineSegment StartX=23.5 StartY=1.5 StartZ=0 EndX=23.5 EndY=-1.5 EndZ=0
    g6: LineSegment StartX=23.5 StartY=-1.5 StartZ=0 EndX=26.5 EndY=-2 EndZ=0
    g7: LineSegment StartX=26.5 StartY=-2 StartZ=0 EndX=28.5 EndY=-2 EndZ=0
  constraints (23):
    c: Coincident(g0,g1)
    c: Vertical(g1)
    c: Coincident(g1,g2)
    c: Symmetric(g0,g2,g-1)
    c: Symmetric(g1,g0,g-1)
    c: DistanceY(g1) = -3
    c: DistanceX(g2,g1) = 3
    c: DistanceX(g-1,g2) = 28.5
    c: Coincident(g0,g3)
    c: Horizontal(g3)
    c: Coincident(g3,g4)
    c: Coincident(g4,g5)
    c: Vertical(g5)
    c: Coincident(g5,g6)
    c: Coincident(g6,g7)
    c: Coincident(g7,g2)
    c: Horizontal(g7)
    c: Symmetric(g3,g6,g-1)
    c: Symmetric(g4,g5,g-1)
    c: DistanceX(g3) = -2
    c: Equal(g1,g5)
    c: DistanceY(g0,g2) = -4
    c: DistanceX(g4,g3) = 3
FEATURE [PartDesign::Pad] Pad010
  Length = 30
  Length2 = 100
  Sketch = -> Sketch008
  Type = 0
FEATURE [Part::FeaturePython] Clone025  label="Clone of Pad002"  # Draft clone (typed FeaturePython)
  Objects = -> [Pad010]
  Placement = pos=(0,0,-15) rot=(0,0,1;0rad)
  Scale = (1,1,1)
FEATURE [Part::FeaturePython] Array001  # Draft array (typed FeaturePython)
  Angle = 360
  ArrayType = 1
  Axis = (0,0,1)
  Base = -> Clone025
  Center = (0,0,0)
  Fuse = false
  IntervalAxis = (0,0,0)
  IntervalX = (1,0,0)
  IntervalY = (0,1,0)
  IntervalZ = (0,0,0)
  NumberPolar = 16
  NumberX = 2
  NumberY = 2
  NumberZ = 1
FEATURE [Part::MultiFuse] Fusion026
  Shapes = -> [Pad009,Array001]
FEATURE [Part::Cut] Cut067
  Base = -> Revolution001
  Tool = -> Fusion025
FEATURE [Part::Cut] Cut068
  Base = -> Cut067
  Tool = -> Fusion026
FEATURE [Part::Fillet] Fillet007  label="ruedaDentServoV2_26"
  Base = -> Cut068
  Edges = 32 edges r=2.6: [Edge68,Edge71,Edge73,Edge79,Edge81,Edge87,Edge89,Edge95,Edge97,Edge103,Edge105,Edge111,Edge113,Edge119,Edge121,Edge127,Edge129,Edge135,Edge137,Edge143,Edge145,Edge151,Edge153,Edge159,Edge161,Edge167,Edge169,Edge175,Edge177,Edge183,Edge185,Edge191]
FEATURE [Part::Cylinder] Cylinder030  label="preTopeCorrea"
  Angle = 360
  Height = 2
  Placement = pos=(0,0,-12) rot=(0,0,1;0rad)
  Radius = 28.5
FEATURE [Part::Cylinder] Cylinder031  label="Taladro"
  Angle = 360
  Height = 10
  Placement = pos=(0,0,-15) rot=(0,0,1;0rad)
  Radius = 4.5
FEATURE [Part::Cut] Cut069  label="tope"
  Base = -> Cylinder030
  Tool = -> Cylinder031
FEATURE [Part::MultiFuse] Fusion027  label="ruedaDentServoV4"
  Shapes = -> [Fillet007,Cut069]
FEATURE [App::DocumentObjectGroup] Grupo007  label="GR_RuedaServo"
  Group = -> [Pad010,Fusion027]
FEATURE [Part::Feature] Fusion029  label="csRuedaDentServoD"
  Placement = pos=(35.6,92,0) rot=(-1,0,0;1.5708rad)
  shape: bbox 57 x 24 x 57 mm, 132 faces (baked)
FEATURE [Part::Feature] Fusion030  label="csRuedaDentServoI"
  Placement = pos=(35.5,-29,0) rot=(0,-0.707107,0.707107;3.14159rad)
  shape: bbox 57 x 24 x 57 mm, 132 faces (baked)
FEATURE [Part::Cylinder] Cylinder032  label="Cilindro035"
  Angle = 360
  Height = 2
  Radius = 28.5
FEATURE [Sketcher::SketchObject] Sketch009
  sketch-geometry (11):
    g0: LineSegment [constr] StartX=-15.0987 StartY=0 StartZ=0 EndX=15.0987 EndY=0 EndZ=0
    g1: ArcOfCircle CenterX=0 CenterY=-16.4544 CenterZ=0 NormalX=0 NormalY=0 NormalZ=1 Radius=22.332 StartAngle=0.828339 EndAngle=1.43871
    g2: ArcOfCircle CenterX=0 CenterY=16.4544 CenterZ=0 NormalX=0 NormalY=0 NormalZ=1 Radius=22.332 StartAngle=3.96993 EndAngle=4.6609
    g3: ArcOfCircle CenterX=0 CenterY=-16.4544 CenterZ=0 NormalX=0 NormalY=0 NormalZ=1 Radius=23.8811 StartAngle=0.748374 EndAngle=2.39322
    g4: ArcOfCircle CenterX=0 CenterY=16.4544 CenterZ=0 NormalX=0 NormalY=0 NormalZ=1 Radius=24.1614 StartAngle=3.90238 EndAngle=4.6648
    g5: ArcOfCircle CenterX=0 CenterY=-16.4544 CenterZ=0 NormalX=0 NormalY=0 NormalZ=1 Radius=22.332 StartAngle=1.70288 EndAngle=2.31325
    g6: LineSegment StartX=-1.1494 StartY=-5.84798 StartZ=0 EndX=-1.1494 EndY=-7.67959 EndZ=0
    g7: LineSegment StartX=1.31676 StartY=-5.83873 StartZ=0 EndX=1.31676 EndY=-7.67104 EndZ=0
    g8: ArcOfCircle CenterX=0 CenterY=16.4544 CenterZ=0 NormalX=0 NormalY=0 NormalZ=1 Radius=22.332 StartAngle=4.77139 EndAngle=5.45485
    g9: ArcOfCircle CenterX=0 CenterY=16.4544 CenterZ=0 NormalX=0 NormalY=0 NormalZ=1 Radius=24.1614 StartAngle=4.76691 EndAngle=5.5224
    g10: ArcOfCircle CenterX=0 CenterY=0.886253 CenterZ=0 NormalX=0 NormalY=0 NormalZ=1 Radius=5.62671 StartAngle=2.12083 EndAngle=7.30395
  constraints (29):
    c: Horizontal(g0)
    c: PointOnObject(g0,g-1)
    c: Coincident(g5,g0)
    c: Coincident(g1,g0)
    c: Equal(g1,g2)
    c: Coincident(g2,g0)
    c: Coincident(g0,g8)
    c: Coincident(g1,g3)
    c: Coincident(g2,g4)
    c: PointOnObject(g2,g-2)
    c: Coincident(g9,g3)
    c: Equal(g1,g5)
    c: Coincident(g1,g5)
    c: PointOnObject(g4,g3)
    c: Coincident(g3,g4)
    c: Vertical(g6)
    c: Parallel(g6,g7)
    c: Equal(g2,g8)
    c: Coincident(g2,g8)
    c: Equal(g4,g9)
    c: Coincident(g4,g9)
    c: Coincident(g6,g4)
    c: Coincident(g7,g9)
    c: Coincident(g7,g8)
    c: Coincident(g6,g2)
    c: DistanceX(g3,g3) = 35
    c: PointOnObject(g10,g-2)
    c: Coincident(g10,g5)
    c: Coincident(g1,g10)
FEATURE [PartDesign::Pad] Pad011  label="ojoMolde"
  Length = 2
  Length2 = 100
  Sketch = -> Sketch009
  Type = 0
FEATURE [Part::Cylinder] Cylinder033  label="Cilindro036"
  Angle = 360
  Height = 10
  Radius = 20
FEATURE [Part::Cylinder] Cylinder034  label="Cilindro037"
  Angle = 360
  Height = 10
  Radius = 19
FEATURE [Part::Cut] Cut070
  Base = -> Cylinder033
  Placement = pos=(0,0,-10) rot=(0,0,1;0rad)
  Tool = -> Cylinder034
FEATURE [Sketcher::SketchObject] Sketch010
  Placement = pos=(0,0,0) rot=(0.57735,0.57735,0.57735;2.0944rad)
  sketch-geometry (3):
    g0: LineSegment StartX=0 StartY=10 StartZ=0 EndX=-5.37675 EndY=-10.0663 EndZ=0
    g1: LineSegment StartX=-5.37675 StartY=-10.0663 StartZ=0 EndX=5.37675 EndY=-10.0663 EndZ=0
    g2: LineSegment StartX=5.37675 StartY=-10.0663 StartZ=0 EndX=0 EndY=10 EndZ=0
  constraints (9):
    c: PointOnObject(g0,g-2)
    c: Coincident(g0,g1)
    c: Horizontal(g1)
    c: Coincident(g1,g2)
    c: Coincident(g2,g0)
    c: Symmetric(g1,g0,g-2)
    c: DistanceY(g-1,g0) = 10
    c: Angle(g0,g2) = 0.523599
    c: DistanceY(g0,g1) = -20.0663
FEATURE [PartDesign::Pad] Pad012  label="Corte"
  Length = 100
  Length2 = 100
  Placement = pos=(0,0,0) rot=(0.57735,0.57735,0.57735;2.0944rad)
  Sketch = -> Sketch010
  Type = 0
FEATURE [Part::FeaturePython] Clone026  label="Clone of Pad"  # Draft clone (typed FeaturePython)
  Objects = -> [Pad012]
  Placement = pos=(-44,0,-10) rot=(0.57735,0.57735,0.57735;2.0944rad)
  Scale = (1,1,1)
FEATURE [Part::FeaturePython] Clone027  label="Clone of Pad003"  # Draft clone (typed FeaturePython)
  Objects = -> [Pad012]
  Placement = pos=(0,-44,-10) rot=(0,0.707107,0.707107;3.14159rad)
  Scale = (1,1,1)
FEATURE [Part::Cut] Cut071
  Base = -> Cut070
  Tool = -> Clone026
FEATURE [Part::Cut] Cut072
  Base = -> Cut071
  Tool = -> Clone027
FEATURE [Part::Feature] Pad013
  Placement = pos=(0,0,-3) rot=(0,0,1;0rad)
  shape: bbox 43.93 x 22.27 x 10 mm, 12 faces (baked)
FEATURE [Part::Offset] Offset  label="Hueco001"
  Fill = false
  Intersection = false
  Join = 2
  Mode = 0
  Placement = pos=(0,0,-3) rot=(0,0,1;0rad)
  SelfIntersection = false
  Source = -> Pad013
  Value = 0.2
FEATURE [Part::Feature] Pad014  label="Pad018"
  Placement = pos=(0,0,-3) rot=(0,0,1;0rad)
  shape: bbox 35 x 15.11 x 10 mm, 12 faces (baked)
FEATURE [Part::Offset] Offset001  label="Hueco"
  Fill = false
  Intersection = false
  Join = 2
  Mode = 0
  Placement = pos=(0,0,-3) rot=(0,0,1;0rad)
  SelfIntersection = false
  Source = -> Pad014
  Value = 0.22
FEATURE [Part::Cut] Cut073
  Base = -> Cylinder032
  Tool = -> Offset001
FEATURE [Part::MultiFuse] Fusion031  label="TapaCubos"
  Placement = pos=(0,0,0) rot=(1,0,0;3.14159rad)
  Shapes = -> [Cut072,Cut073]
FEATURE [Part::Cylinder] Cylinder035  label="Cilindro038"
  Angle = 360
  Height = 0.8
  Radius = 18.7
FEATURE [Part::Feature] Pad015  label="Pieza"
  Placement = pos=(0,0,0.8) rot=(0,0,1;0rad)
  shape: bbox 35 x 15.11 x 2 mm, 12 faces (baked)
FEATURE [Part::MultiFuse] Fusion032  label="Decoracion"
  Placement = pos=(0,0,0.8) rot=(1,0,0;3.14159rad)
  Shapes = -> [Cylinder035,Pad015]
FEATURE [App::DocumentObjectGroup] Grupo008  label="GR_TapaCubos"
  Group = -> [Pad011,Pad012,Offset,Fusion031,Fusion032]
FEATURE [Part::Feature] Fusion033  label="csOjoDecoracionI"
  Placement = pos=(35.5,-41,0) rot=(1,0,0;1.5708rad)
  shape: bbox 37.4 x 2.8 x 37.4 mm, 14 faces (baked)
FEATURE [Part::Feature] Fusion034  label="csTapaCubosI"
  Placement = pos=(35.5,-41,0) rot=(1,0,0;1.5708rad)
  shape: bbox 57 x 12 x 57 mm, 34 faces (baked)
FEATURE [Part::Feature] Fusion035  label="csOjoDecoracionD"
  Placement = pos=(35.6,104,0) rot=(0,0.707107,0.707107;3.14159rad)
  shape: bbox 37.4 x 2.8 x 37.4 mm, 14 faces (baked)
FEATURE [Part::Feature] Fusion036  label="csTapaCubosD"
  Placement = pos=(35.6,104,0) rot=(0,0.707107,0.707107;3.14159rad)
  shape: bbox 57 x 12 x 57 mm, 34 faces (baked)
FEATURE [Part::Feature] Compound004  label="battery-holder001"
  Placement = pos=(26,34,28) rot=(0,0,1;1.5708rad)
  shape: bbox 60.07 x 51.23 x 30.51 mm, 1148 faces, 59 solids (baked)
FEATURE [Mesh::Feature] zum_bt_  label="zum_bt_328"
  Placement = pos=(59,58,50) rot=(0,0,1;3.14159rad)
FEATURE [App::DocumentObjectGroup] Grupo009  label="NoImprimibles"
  Group = -> [Compound,Compound001,Compound002,Compound003,Fusion024,Compound004,zum_bt_]
FEATURE [Sketcher::SketchObject] Sketch011
  sketch-geometry (2):
    g0: Circle CenterX=0 CenterY=0 CenterZ=0 NormalX=0 NormalY=0 NormalZ=1 Radius=52.6
    g1: Circle CenterX=0 CenterY=0 CenterZ=0 NormalX=0 NormalY=0 NormalZ=1 Radius=50.6
  constraints (4):
    c: Coincident(g0,g-1)
    c: Radius(g0) = 52.6
    c: Coincident(g1,g-1)
    c: Radius(g1) = 50.6
FEATURE [PartDesign::Pad] Pad016  label="Pad019"
  Length = 20
  Length2 = 100
  Sketch = -> Sketch011
  Type = 0
FEATURE [Sketcher::SketchObject] Sketch012
  sketch-geometry (8):
    g0: LineSegment StartX=52.6 StartY=1.75 StartZ=0 EndX=54.6 EndY=1.25 EndZ=0
    g1: LineSegment StartX=54.6 StartY=1.25 StartZ=0 EndX=54.6 EndY=-1.25 EndZ=0
    g2: LineSegment StartX=54.6 StartY=-1.25 StartZ=0 EndX=52.6 EndY=-1.75 EndZ=0
    g3: LineSegment StartX=52.6 StartY=1.75 StartZ=0 EndX=50.6 EndY=1.75 EndZ=0
    g4: LineSegment StartX=50.6 StartY=1.75 StartZ=0 EndX=48.6 EndY=1.25 EndZ=0
    g5: LineSegment StartX=48.6 StartY=1.25 StartZ=0 EndX=48.6 EndY=-1.25 EndZ=0
    g6: LineSegment StartX=48.6 StartY=-1.25 StartZ=0 EndX=50.6 EndY=-1.75 EndZ=0
    g7: LineSegment StartX=50.6 StartY=-1.75 StartZ=0 EndX=52.6 EndY=-1.75 EndZ=0
  constraints (23):
    c: Coincident(g0,g1)
    c: Vertical(g1)
    c: Coincident(g1,g2)
    c: Symmetric(g0,g2,g-1)
    c: Symmetric(g1,g0,g-1)
    c: DistanceY(g1) = -2.5
    c: DistanceX(g2,g1) = 2
    c: DistanceX(g-1,g2) = 52.6
    c: Coincident(g0,g3)
    c: Horizontal(g3)
    c: Coincident(g3,g4)
    c: Coincident(g4,g5)
    c: Vertical(g5)
    c: Coincident(g5,g6)
    c: Coincident(g6,g7)
    c: Coincident(g7,g2)
    c: Horizontal(g7)
    c: Symmetric(g3,g6,g-1)
    c: Symmetric(g4,g5,g-1)
    c: DistanceX(g3) = -2
    c: Equal(g1,g5)
    c: DistanceY(g0,g2) = -3.5
    c: DistanceX(g4,g3) = 2
FEATURE [PartDesign::Pad] Pad017
  Length = 20
  Length2 = 100
  Sketch = -> Sketch012
  Type = 0
FEATURE [Part::FeaturePython] Array002  # Draft array (typed FeaturePython)
  Angle = 360
  ArrayType = 1
  Axis = (0,0,1)
  Base = -> Pad017
  Center = (0,0,0)
  Fuse = false
  IntervalAxis = (0,0,0)
  IntervalX = (1,0,0)
  IntervalY = (0,1,0)
  IntervalZ = (0,0,0)
  NumberPolar = 31
  NumberX = 2
  NumberY = 2
  NumberZ = 1
FEATURE [Part::MultiFuse] Fusion037  label="RuedaOruga31"
  Shapes = -> [Pad016,Array002]
FEATURE [App::DocumentObjectGroup] Grupo010  label="GR_Orugas"
  Group = -> [Fusion037]
FEATURE [Part::Feature] Fusion038  label="csRuedaOruga31"
  Placement = pos=(8,-159,-28) rot=(0,0,1;0rad)
  shape: bbox 109 x 109.2 x 20 mm, 312 faces (baked)
FEATURE [Sketcher::SketchObject] Sketch013
  sketch-geometry (10):
    g0: LineSegment StartX=-2.40769 StartY=1.98255 StartZ=0 EndX=5.59231 EndY=1.98255 EndZ=0
    g1: LineSegment StartX=5.59231 StartY=1.98255 StartZ=0 EndX=5.59231 EndY=-2.21745 EndZ=0
    g2: LineSegment StartX=5.59231 StartY=-2.21745 StartZ=0 EndX=-14.4077 EndY=-2.21745 EndZ=0
    g3: LineSegment StartX=-14.4077 StartY=-2.21745 StartZ=0 EndX=-14.4077 EndY=-5.21745 EndZ=0
    g4: LineSegment StartX=-14.4077 StartY=-5.21745 StartZ=0 EndX=8.59231 EndY=-5.21745 EndZ=0
    g5: LineSegment StartX=8.59231 StartY=-5.21745 StartZ=0 EndX=8.59231 EndY=4.98255 EndZ=0
    g6: LineSegment StartX=8.59231 StartY=4.98255 StartZ=0 EndX=2.59231 EndY=4.98255 EndZ=0
    g7: LineSegment StartX=-2.40769 StartY=1.98255 StartZ=0 EndX=-2.40769 EndY=11.9826 EndZ=0
    g8: LineSegment StartX=-2.40769 StartY=11.9826 StartZ=0 EndX=2.59231 EndY=11.9826 EndZ=0
    g9: LineSegment StartX=2.59231 StartY=11.9826 StartZ=0 EndX=2.59231 EndY=4.98255 EndZ=0
  constraints (29):
    c: Horizontal(g0)
    c: Coincident(g0,g1)
    c: Vertical(g1)
    c: Coincident(g1,g2)
    c: Horizontal(g2)
    c: Vertical(g3)
    c: Coincident(g3,g4)
    c: Horizontal(g4)
    c: Coincident(g4,g5)
    c: Vertical(g5)
    c: Coincident(g5,g6)
    c: Horizontal(g6)
    c: DistanceY(g3) = -3
    c: DistanceY(g1,g4) = -3
    c: DistanceY(g1) = -4.2
    c: DistanceX(g0,g5) = 3
    c: DistanceX(g4) = 23
    c: DistanceX(g0,g0) = 8
    c: Coincident(g2,g3)
    c: Vertical(g7)
    c: Coincident(g7,g8)
    c: Horizontal(g8)
    c: Coincident(g8,g9)
    c: Vertical(g9)
    c: Coincident(g6,g9)
    c: DistanceY(g0,g5) = 3
    c: DistanceX(g8) = 5
    c: Coincident(g7,g0)
    c: DistanceY(g7) = 10
FEATURE [PartDesign::Pad] Pad018  label="Tope"
  Length = 8
  Length2 = 100
  Sketch = -> Sketch013
  Type = 0
FEATURE [Part::Feature] Pad019  label="csTopePilas"
  Placement = pos=(55.3577,35.5,13.0174) rot=(1,0,0;1.5708rad)
  shape: bbox 23 x 8 x 17.2 mm, 12 faces (baked)
FEATURE [App::DocumentObjectGroup] Grupo011  label="GR_TopePilas"
  Group = -> [Pad018]
